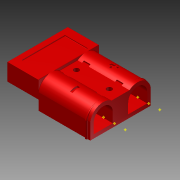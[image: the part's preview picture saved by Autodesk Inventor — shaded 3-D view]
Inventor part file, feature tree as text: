
AUTODESK INVENTOR PART (.ipt)
format: ipt  version: 2011 (Build 150239000, 239)  size: 387,584 bytes
history: native  units: mm
features: other x8, sketch x2, plane x2, imported_body x1
ambient origin geometry x8: Origin, YZ Plane, XZ Plane, XY Plane, X Axis, Y Axis, Z Axis, Center Point
bodies: Solid1 (feature_tree)
feature tree (13):
  imported_body  "Base1"
  sketch  "Sketch1"  dims[d0=6.35mm]
  sketch  "Sketch2"  dims[d1=12.7mm]
  plane  "Work Plane1"
  other  "Work Point3"
  plane  "Work Plane2"
  other  "Work Point4"
  other  "Work Point5"
  other  "Work Point6"
  other  "Work Axis1"
  other  "Work Axis2"
  other  "Work Axis3"
  other  "Work Axis4"
